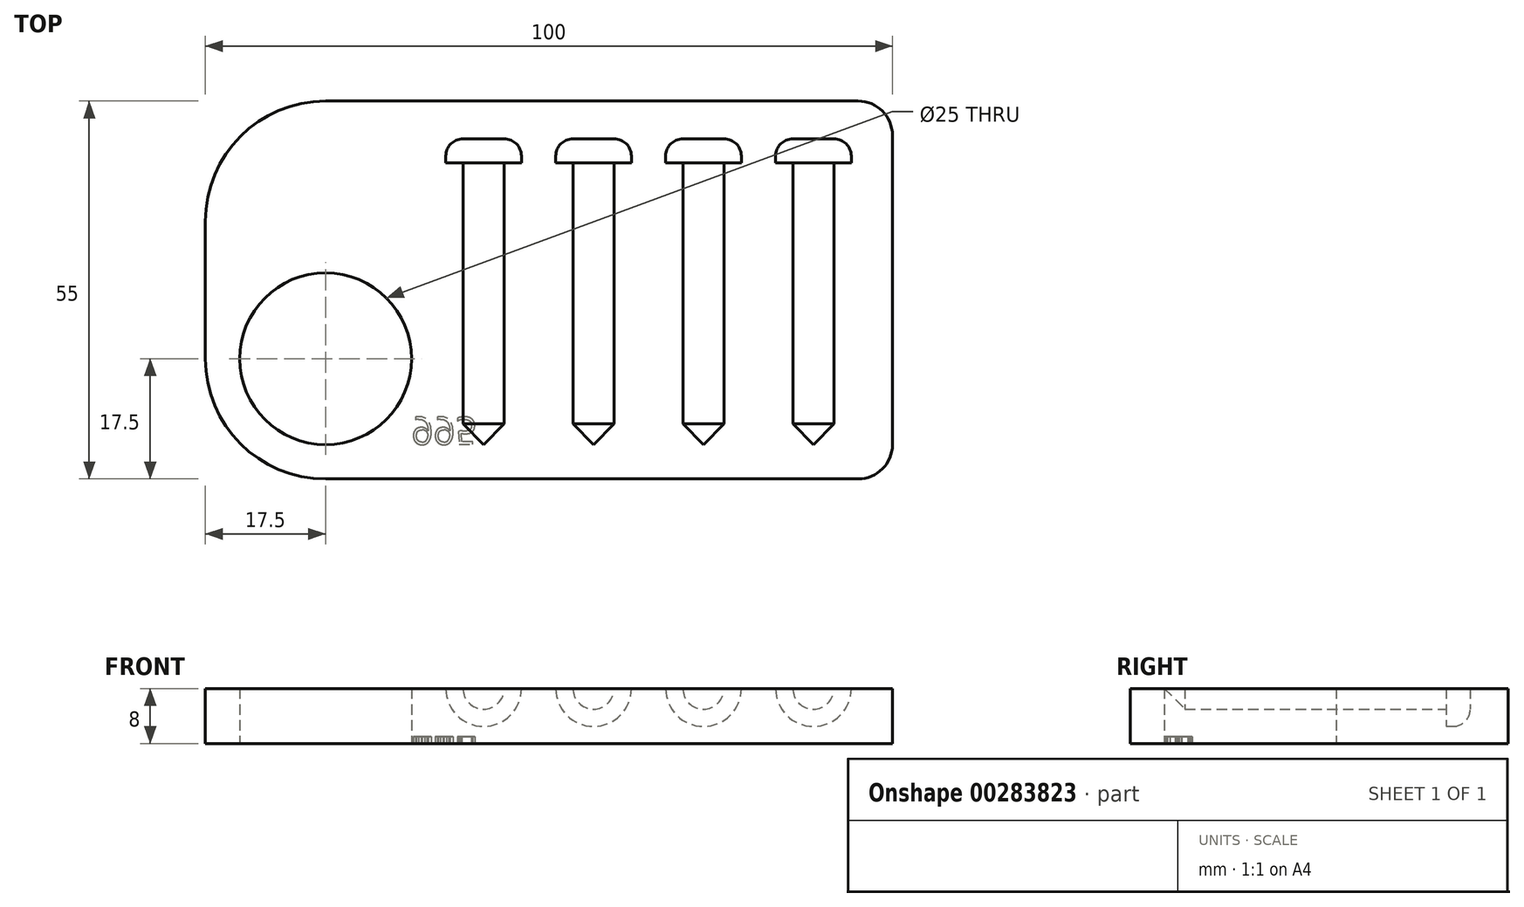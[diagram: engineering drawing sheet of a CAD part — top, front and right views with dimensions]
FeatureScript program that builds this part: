
annotation { "Feature Type Name" : "Feature", "Feature Type Description" : "" }
export const myFeature = defineFeature(function(context is Context, id is Id, definition is map)
    precondition{}
    {
        {
            var Q0;
            Q0=qCreatedBy(makeId("Top.planeOp"),FACE);
            var sketch = newSketch(context, id + "F0", { "sketchPlane" : qUnion([Q0])});
            skLineSegment(sketch, "E0.bottom", {"start": v(17.5, 0) * mm, "end": v(95, 0) * mm});
            skLineSegment(sketch, "E0.top", {"start": v(17.5, 55) * mm, "end": v(95, 55) * mm});
            skLineSegment(sketch, "E0.left", {"start": v(0, 17.5) * mm, "end": v(0, 37.5) * mm});
            skLineSegment(sketch, "E0.right", {"start": v(100, 5) * mm, "end": v(100, 50) * mm});
            skLineSegment(sketch, "E1.bottom", {"start": v(0, 0) * mm, "end": v(17.5, 0) * mm, "construction": true});
            skLineSegment(sketch, "E1.top", {"start": v(0, 17.5) * mm, "end": v(17.5, 17.5) * mm, "construction": true});
            skLineSegment(sketch, "E1.left", {"start": v(0, 0) * mm, "end": v(0, 17.5) * mm, "construction": true});
            skLineSegment(sketch, "E1.right", {"start": v(17.5, 0) * mm, "end": v(17.5, 17.5) * mm, "construction": true});
            skCircle(sketch, "E2", {"center": v(17.5, 17.5) * mm, "radius": 12.5 * mm});
            skPoint(sketch, "E3.visualSharp", {"position": v(0, 0) * mm});
            skArc(sketch, "E3.filletArc", {"start": v(0, 17.5) * mm, "mid": v(5.13, 5.13) * mm, "end": v(17.5, 0) * mm});
            skPoint(sketch, "E4.visualSharp", {"position": v(0, 55) * mm});
            skArc(sketch, "E4.filletArc", {"start": v(17.5, 55) * mm, "mid": v(5.13, 49.87) * mm, "end": v(0, 37.5) * mm});
            skPoint(sketch, "E5.visualSharp", {"position": v(100, 55) * mm});
            skArc(sketch, "E5.filletArc", {"start": v(100, 50) * mm, "mid": v(98.54, 53.54) * mm, "end": v(95, 55) * mm});
            skPoint(sketch, "E6.visualSharp", {"position": v(100, 0) * mm});
            skArc(sketch, "E6.filletArc", {"start": v(95, 0) * mm, "mid": v(98.54, 1.46) * mm, "end": v(100, 5) * mm});
            skSolve(sketch);
        }
        {
            var Q0;
            Q0=makeQuery(id+"F0.imprint","IMPRINT",FACE,{"disambiguationData":[TD([[makeQuery(id+"F0.imprint","IMPRINT",EDGE,{"derivedFrom":sQuery(id+"F0.wireOp",EDGE,"E0.bottom")}),1.0]])]});
            extrude(context, id + "F1", {"entities" : qUnion([Q0]), "depth" : 8 * mm});
        }
        {
            var Q0;
            Q0=makeQuery(id+"F1.opExtrude","CAP_FACE",FACE,{"disambiguationData":[OSD([sQuery(id+"F0.wireOp",EDGE,"E0.bottom"),sQuery(id+"F0.wireOp",EDGE,"E0.top"),sQuery(id+"F0.wireOp",EDGE,"E0.left"),sQuery(id+"F0.wireOp",EDGE,"E0.right"),sQuery(id+"F0.wireOp",EDGE,"E2"),sQuery(id+"F0.wireOp",EDGE,"E3.filletArc"),sQuery(id+"F0.wireOp",EDGE,"E4.filletArc"),sQuery(id+"F0.wireOp",EDGE,"E5.filletArc"),sQuery(id+"F0.wireOp",EDGE,"E6.filletArc")])],"isStart":false});
            var sketch = newSketch(context, id + "F2", { "sketchPlane" : qUnion([Q0])});
            skLineSegment(sketch, "E7.bottom", {"start": v(0, 0) * mm, "end": v(40.5, 0) * mm, "construction": true});
            skLineSegment(sketch, "E7.top", {"start": v(0, 5) * mm, "end": v(40.5, 5) * mm, "construction": true});
            skLineSegment(sketch, "E7.left", {"start": v(0, 0) * mm, "end": v(0, 5) * mm, "construction": true});
            skLineSegment(sketch, "E7.right", {"start": v(40.5, 0) * mm, "end": v(40.5, 5) * mm, "construction": true});
            skLineSegment(sketch, "E8.left", {"start": v(40.5, 5) * mm, "end": v(40.5, 46) * mm});
            skLineSegment(sketch, "E8.right", {"start": v(43.5, 8) * mm, "end": v(43.5, 46) * mm});
            skLineSegment(sketch, "E9.bottom", {"start": v(43.5, 46) * mm, "end": v(46, 46) * mm});
            skLineSegment(sketch, "E9.top", {"start": v(40.5, 49.5) * mm, "end": v(43.5, 49.5) * mm});
            skLineSegment(sketch, "E9.left", {"start": v(40.5, 46) * mm, "end": v(40.5, 49.5) * mm});
            skLineSegment(sketch, "E9.right", {"start": v(46, 46) * mm, "end": v(46, 47) * mm});
            skPoint(sketch, "E10.visualSharp", {"position": v(46, 49.5) * mm});
            skArc(sketch, "E10.filletArc", {"start": v(46, 47) * mm, "mid": v(45.27, 48.77) * mm, "end": v(43.5, 49.5) * mm});
            skLineSegment(sketch, "E11", {"start": v(43.5, 8) * mm, "end": v(40.5, 5) * mm});
            skLineSegment(sketch, "E12", {"start": v(40.5, 5) * mm, "end": v(56.5, 5) * mm, "construction": true});
            skLineSegment(sketch, "E13", {"start": v(56.5, 5) * mm, "end": v(72.5, 5) * mm, "construction": true});
            skLineSegment(sketch, "E14", {"start": v(72.5, 5) * mm, "end": v(88.5, 5) * mm, "construction": true});
            skLineSegment(sketch, "E15.left", {"start": v(56.5, 5) * mm, "end": v(56.5, 46) * mm});
            skLineSegment(sketch, "E15.right", {"start": v(59.5, 8) * mm, "end": v(59.5, 46) * mm});
            skLineSegment(sketch, "E16.bottom", {"start": v(59.5, 46) * mm, "end": v(62, 46) * mm});
            skLineSegment(sketch, "E16.top", {"start": v(56.5, 49.5) * mm, "end": v(59.5, 49.5) * mm});
            skLineSegment(sketch, "E16.left", {"start": v(56.5, 46) * mm, "end": v(56.5, 49.5) * mm});
            skLineSegment(sketch, "E16.right", {"start": v(62, 46) * mm, "end": v(62, 47) * mm});
            skPoint(sketch, "E17.visualSharp", {"position": v(62, 49.5) * mm});
            skArc(sketch, "E17.filletArc", {"start": v(62, 47) * mm, "mid": v(61.27, 48.77) * mm, "end": v(59.5, 49.5) * mm});
            skLineSegment(sketch, "E18", {"start": v(59.5, 8) * mm, "end": v(56.5, 5) * mm});
            skLineSegment(sketch, "E19.left", {"start": v(72.5, 5) * mm, "end": v(72.5, 46) * mm});
            skLineSegment(sketch, "E19.right", {"start": v(75.5, 8) * mm, "end": v(75.5, 46) * mm});
            skLineSegment(sketch, "E20.bottom", {"start": v(75.5, 46) * mm, "end": v(78, 46) * mm});
            skLineSegment(sketch, "E20.top", {"start": v(72.5, 49.5) * mm, "end": v(75.5, 49.5) * mm});
            skLineSegment(sketch, "E20.left", {"start": v(72.5, 46) * mm, "end": v(72.5, 49.5) * mm});
            skLineSegment(sketch, "E20.right", {"start": v(78, 46) * mm, "end": v(78, 47) * mm});
            skPoint(sketch, "E21.visualSharp", {"position": v(78, 49.5) * mm});
            skArc(sketch, "E21.filletArc", {"start": v(78, 47) * mm, "mid": v(77.27, 48.77) * mm, "end": v(75.5, 49.5) * mm});
            skLineSegment(sketch, "E22", {"start": v(75.5, 8) * mm, "end": v(72.5, 5) * mm});
            skLineSegment(sketch, "E23.left", {"start": v(88.5, 5) * mm, "end": v(88.5, 46) * mm});
            skLineSegment(sketch, "E23.right", {"start": v(91.5, 8) * mm, "end": v(91.5, 46) * mm});
            skLineSegment(sketch, "E24.bottom", {"start": v(91.5, 46) * mm, "end": v(94, 46) * mm});
            skLineSegment(sketch, "E24.top", {"start": v(88.5, 49.5) * mm, "end": v(91.5, 49.5) * mm});
            skLineSegment(sketch, "E24.left", {"start": v(88.5, 46) * mm, "end": v(88.5, 49.5) * mm});
            skLineSegment(sketch, "E24.right", {"start": v(94, 46) * mm, "end": v(94, 47) * mm});
            skPoint(sketch, "E25.visualSharp", {"position": v(94, 49.5) * mm});
            skArc(sketch, "E25.filletArc", {"start": v(94, 47) * mm, "mid": v(93.27, 48.77) * mm, "end": v(91.5, 49.5) * mm});
            skLineSegment(sketch, "E26", {"start": v(91.5, 8) * mm, "end": v(88.5, 5) * mm});
            skSolve(sketch);
        }
        {
            var Q0;
            Q0=makeQuery(id+"F2.imprint","IMPRINT",FACE,{"disambiguationData":[TD([[makeQuery(id+"F2.imprint","IMPRINT",EDGE,{"derivedFrom":sQuery(id+"F2.wireOp",EDGE,"E8.left")}),-1.0]])]});
            var Q1;
            Q1=sQuery(id+"F2.wireOp",EDGE,"E8.left");
            revolve(context, id + "F3", {"operationType" : NewBodyOperationType.REMOVE, "entities" : qUnion([Q0]), "axis" : qUnion([Q1]), "revolveType" : RevolveType.FULL, "oppositeDirection" : true});
        }
        {
            var Q0;
            Q0=makeQuery(id+"F2.imprint","IMPRINT",FACE,{"disambiguationData":[TD([[makeQuery(id+"F2.imprint","IMPRINT",EDGE,{"derivedFrom":sQuery(id+"F2.wireOp",EDGE,"E15.left")}),-1.0]])]});
            var Q1;
            Q1=sQuery(id+"F2.wireOp",EDGE,"E15.left");
            revolve(context, id + "F4", {"operationType" : NewBodyOperationType.REMOVE, "entities" : qUnion([Q0]), "axis" : qUnion([Q1]), "revolveType" : RevolveType.FULL, "oppositeDirection" : true});
        }
        {
            var Q0;
            Q0=makeQuery(id+"F2.imprint","IMPRINT",FACE,{"disambiguationData":[TD([[makeQuery(id+"F2.imprint","IMPRINT",EDGE,{"derivedFrom":sQuery(id+"F2.wireOp",EDGE,"E19.left")}),-1.0]])]});
            var Q1;
            Q1=sQuery(id+"F2.wireOp",EDGE,"E19.left");
            revolve(context, id + "F5", {"operationType" : NewBodyOperationType.REMOVE, "entities" : qUnion([Q0]), "axis" : qUnion([Q1]), "revolveType" : RevolveType.FULL, "oppositeDirection" : true});
        }
        {
            var Q0;
            Q0=makeQuery(id+"F2.imprint","IMPRINT",FACE,{"disambiguationData":[TD([[makeQuery(id+"F2.imprint","IMPRINT",EDGE,{"derivedFrom":sQuery(id+"F2.wireOp",EDGE,"E23.left")}),-1.0]])]});
            var Q1;
            Q1=sQuery(id+"F2.wireOp",EDGE,"E23.left");
            revolve(context, id + "F6", {"operationType" : NewBodyOperationType.REMOVE, "entities" : qUnion([Q0]), "axis" : qUnion([Q1]), "revolveType" : RevolveType.FULL, "oppositeDirection" : true});
        }
        {
            var Q0;
            Q0=makeQuery(id+"F1.opExtrude","CAP_FACE",FACE,{"disambiguationData":[OSD([sQuery(id+"F0.wireOp",EDGE,"E0.bottom"),sQuery(id+"F0.wireOp",EDGE,"E0.top"),sQuery(id+"F0.wireOp",EDGE,"E0.left"),sQuery(id+"F0.wireOp",EDGE,"E0.right"),sQuery(id+"F0.wireOp",EDGE,"E2"),sQuery(id+"F0.wireOp",EDGE,"E3.filletArc"),sQuery(id+"F0.wireOp",EDGE,"E4.filletArc"),sQuery(id+"F0.wireOp",EDGE,"E5.filletArc"),sQuery(id+"F0.wireOp",EDGE,"E6.filletArc")])],"isStart":true});
            var sketch = newSketch(context, id + "F7", { "sketchPlane" : qUnion([Q0])});
            skLineSegment(sketch, "E27.bottom", {"start": v(0, 0) * mm, "end": v(30, 0) * mm, "construction": true});
            skLineSegment(sketch, "E27.top", {"start": v(0, -5) * mm, "end": v(30, -5) * mm, "construction": true});
            skLineSegment(sketch, "E27.left", {"start": v(0, 0) * mm, "end": v(0, -5) * mm, "construction": true});
            skLineSegment(sketch, "E27.right", {"start": v(30, 0) * mm, "end": v(30, -5) * mm, "construction": true});
            skText(sketch, "E28", { "text": "995", "fontName": "OpenSans-Regular.ttf"});
            const initialGuessF7  = {"E28": [0.03, -0.009, 1, 0, 0.004]};
            skSetInitialGuess(sketch, initialGuessF7);
            skSolve(sketch);
        }
        {
            var Q0;
            Q0 = qSketchRegion(id + "F7", true);
            extrude(context, id + "F8", {"entities" : qUnion([Q0]), "operationType" : NewBodyOperationType.REMOVE, "oppositeDirection" : true, "depth" : 1 * mm});
        }
    });
